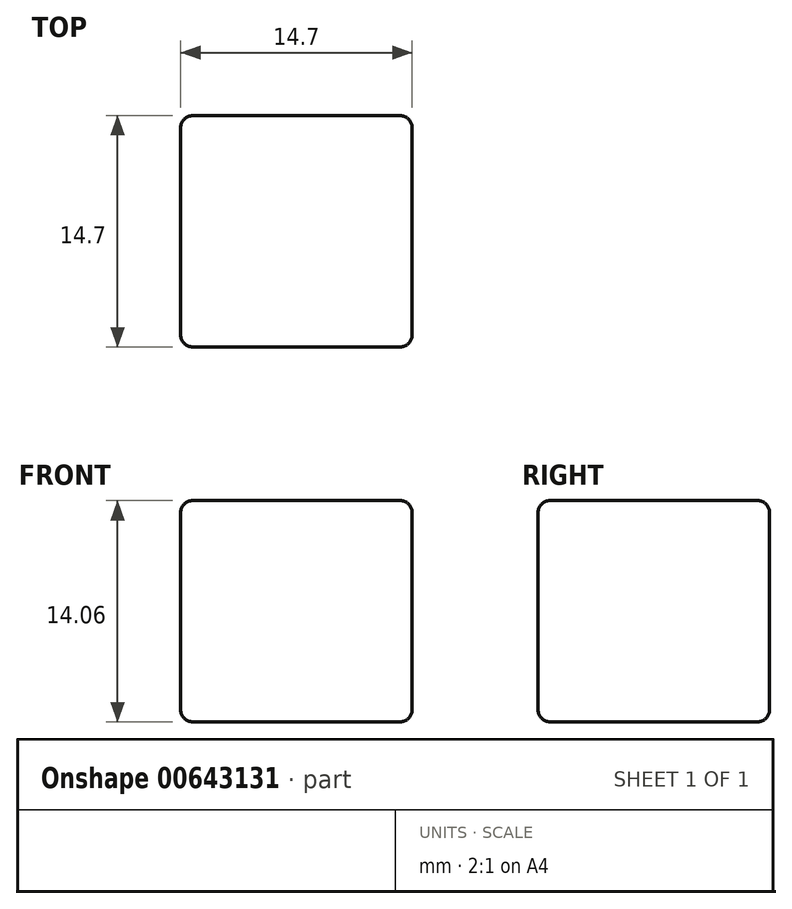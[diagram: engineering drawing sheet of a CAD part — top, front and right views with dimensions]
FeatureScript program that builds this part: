
annotation { "Feature Type Name" : "Feature", "Feature Type Description" : "" }
export const myFeature = defineFeature(function(context is Context, id is Id, definition is map)
    precondition{}
    {
        {
            var Q0;
            Q0=qCreatedBy(makeId("Top.planeOp"),FACE);
            var sketch = newSketch(context, id + "F0", { "sketchPlane" : qUnion([Q0])});
            skLineSegment(sketch, "E0.bottom", {"start": v(-7.35, 7.35) * mm, "end": v(7.35, 7.35) * mm});
            skLineSegment(sketch, "E0.top", {"start": v(-7.35, -7.35) * mm, "end": v(7.35, -7.35) * mm});
            skLineSegment(sketch, "E0.left", {"start": v(-7.35, 7.35) * mm, "end": v(-7.35, -7.35) * mm});
            skLineSegment(sketch, "E0.right", {"start": v(7.35, 7.35) * mm, "end": v(7.35, -7.35) * mm});
            skPoint(sketch, "E0.middle", {"position": v(0, 0) * mm});
            skSolve(sketch);
        }
        {
            var Q0;
            Q0 = qSketchRegion(id + "F0", true);
            extrude(context, id + "F1", {"entities" : qUnion([Q0]), "depth" : 14.06 * mm, "offsetDistance" : 25.4 * mm});
        }
        {
            var Q0;
            Q0=makeQuery(id+"F1.opExtrude","SWEPT_FACE",FACE,{"disambiguationData":[OSD([sQuery(id+"F0.wireOp",EDGE,"E0.top")])]});
            var Q1;
            Q1=makeQuery(id+"F1.opExtrude","SWEPT_EDGE",EDGE,{"disambiguationData":[OSD([sQuery(id+"F0.wireOp",EDGE,"E0.top"),sQuery(id+"F0.wireOp",EDGE,"E0.right")])]});
            var Q2;
            Q2=makeQuery(id+"F1.opExtrude","CAP_FACE",FACE,{"disambiguationData":[OSD([sQuery(id+"F0.wireOp",EDGE,"E0.bottom"),sQuery(id+"F0.wireOp",EDGE,"E0.top"),sQuery(id+"F0.wireOp",EDGE,"E0.left"),sQuery(id+"F0.wireOp",EDGE,"E0.right")])],"isStart":false});
            var Q3;
            Q3=makeQuery(id+"F1.opExtrude","SWEPT_EDGE",EDGE,{"disambiguationData":[OSD([sQuery(id+"F0.wireOp",EDGE,"E0.top"),sQuery(id+"F0.wireOp",EDGE,"E0.left")])]});
            var Q4;
            Q4=makeQuery(id+"F1.opExtrude","CAP_FACE",FACE,{"disambiguationData":[OSD([sQuery(id+"F0.wireOp",EDGE,"E0.bottom"),sQuery(id+"F0.wireOp",EDGE,"E0.top"),sQuery(id+"F0.wireOp",EDGE,"E0.left"),sQuery(id+"F0.wireOp",EDGE,"E0.right")])],"isStart":true});
            var Q5;
            Q5=makeQuery(id+"F1.opExtrude","SWEPT_EDGE",EDGE,{"disambiguationData":[OSD([sQuery(id+"F0.wireOp",EDGE,"E0.bottom"),sQuery(id+"F0.wireOp",EDGE,"E0.right")])]});
            var Q6;
            Q6=makeQuery(id+"F1.opExtrude","SWEPT_FACE",FACE,{"disambiguationData":[OSD([sQuery(id+"F0.wireOp",EDGE,"E0.bottom")])]});
            var Q7;
            Q7=makeQuery(id+"F1.opExtrude","SWEPT_FACE",FACE,{"disambiguationData":[OSD([sQuery(id+"F0.wireOp",EDGE,"E0.left")])]});
            var Q8;
            Q8=makeQuery(id+"F1.opExtrude","SWEPT_FACE",FACE,{"disambiguationData":[OSD([sQuery(id+"F0.wireOp",EDGE,"E0.right")])]});
            var Q9;
            Q9=makeQuery(id+"F1.opExtrude","CAP_EDGE",EDGE,{"disambiguationData":[OSD([sQuery(id+"F0.wireOp",EDGE,"E0.right")])],"isStart":false});
            var Q10;
            Q10=makeQuery(id+"F1.opExtrude","SWEPT_EDGE",EDGE,{"disambiguationData":[OSD([sQuery(id+"F0.wireOp",EDGE,"E0.bottom"),sQuery(id+"F0.wireOp",EDGE,"E0.left")])]});
            var Q11;
            Q11=makeQuery(id+"F1.opExtrude","CAP_EDGE",EDGE,{"disambiguationData":[OSD([sQuery(id+"F0.wireOp",EDGE,"E0.bottom")])],"isStart":true});
            var Q12;
            Q12=makeQuery(id+"F1.opExtrude","CAP_EDGE",EDGE,{"disambiguationData":[OSD([sQuery(id+"F0.wireOp",EDGE,"E0.bottom")])],"isStart":false});
            var Q13;
            Q13=makeQuery(id+"F1.opExtrude","CAP_EDGE",EDGE,{"disambiguationData":[OSD([sQuery(id+"F0.wireOp",EDGE,"E0.top")])],"isStart":true});
            var Q14;
            Q14=makeQuery(id+"F1.opExtrude","CAP_EDGE",EDGE,{"disambiguationData":[OSD([sQuery(id+"F0.wireOp",EDGE,"E0.top")])],"isStart":false});
            var Q15;
            Q15=makeQuery(id+"F1.opExtrude","CAP_EDGE",EDGE,{"disambiguationData":[OSD([sQuery(id+"F0.wireOp",EDGE,"E0.left")])],"isStart":true});
            var Q16;
            Q16=makeQuery(id+"F1.opExtrude","CAP_EDGE",EDGE,{"disambiguationData":[OSD([sQuery(id+"F0.wireOp",EDGE,"E0.left")])],"isStart":false});
            var Q17;
            Q17=makeQuery(id+"F1.opExtrude","CAP_EDGE",EDGE,{"disambiguationData":[OSD([sQuery(id+"F0.wireOp",EDGE,"E0.right")])],"isStart":true});
            fillet(context, id + "F2", {"entities" : qUnion([Q0, Q1, Q2, Q3, Q4, Q5, Q6, Q7, Q8, Q9, Q10, Q11, Q12, Q13, Q14, Q15, Q16, Q17]), "radius" : 0.76 * mm, "tangentPropagation" : true, "allowEdgeOverflow" : false});
        }
    });
